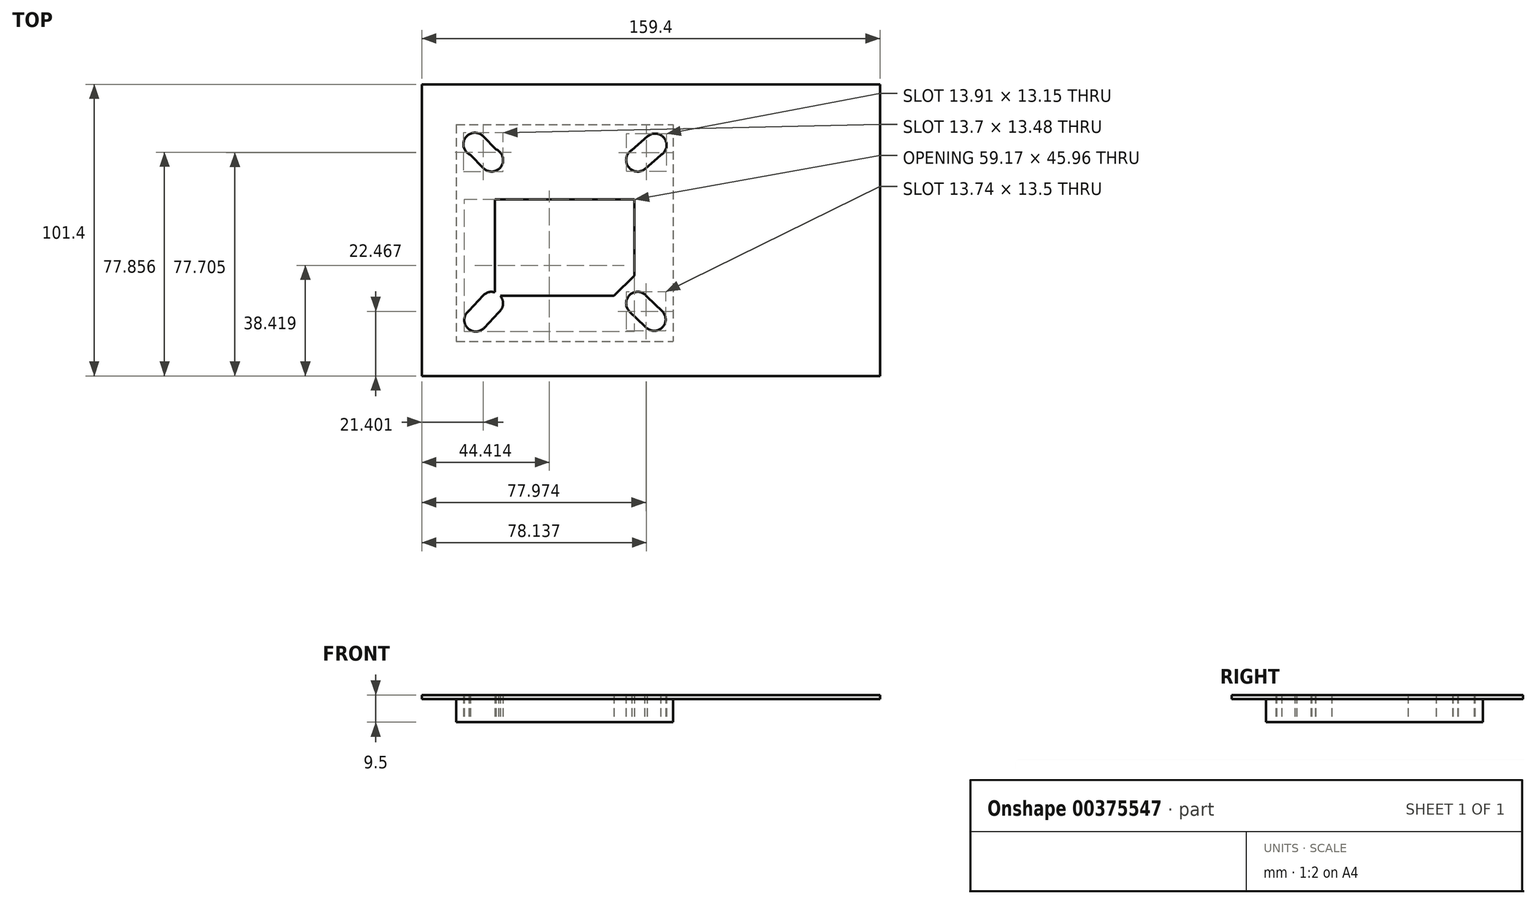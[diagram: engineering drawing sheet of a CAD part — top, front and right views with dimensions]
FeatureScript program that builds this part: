
annotation { "Feature Type Name" : "Feature", "Feature Type Description" : "" }
export const myFeature = defineFeature(function(context is Context, id is Id, definition is map)
    precondition{}
    {
        {
            var Q0;
            Q0=qCreatedBy(makeId("Top.planeOp"),FACE);
            var sketch = newSketch(context, id + "F0", { "sketchPlane" : qUnion([Q0])});
            skLineSegment(sketch, "E0.bottom", {"start": v(-37.22, 52.6) * mm, "end": v(38.18, 52.6) * mm});
            skLineSegment(sketch, "E0.top", {"start": v(-37.22, -22.8) * mm, "end": v(38.18, -22.8) * mm});
            skLineSegment(sketch, "E0.left", {"start": v(-37.22, 52.6) * mm, "end": v(-37.22, -22.8) * mm});
            skLineSegment(sketch, "E0.right", {"start": v(38.18, 52.6) * mm, "end": v(38.18, -22.8) * mm});
            skLineSegment(sketch, "E1.bottom", {"start": v(-23.82, 26.6) * mm, "end": v(24.78, 26.6) * mm});
            skLineSegment(sketch, "E1.left", {"start": v(-23.82, 26.6) * mm, "end": v(-23.82, -6.93) * mm});
            skCircle(sketch, "E2", {"center": v(-24.92, 40.3) * mm, "radius": 4 * mm});
            skCircle(sketch, "E3", {"center": v(25.88, 40.3) * mm, "radius": 4 * mm});
            skCircle(sketch, "E4", {"center": v(25.88, -9.56) * mm, "radius": 4 * mm});
            skCircle(sketch, "E5", {"center": v(-24.92, -9.56) * mm, "radius": 4 * mm});
            skLineSegment(sketch, "E6", {"start": v(24.78, 0) * mm, "end": v(17.57, -6.93) * mm});
            skLineSegment(sketch, "E7", {"start": v(24.78, 26.6) * mm, "end": v(24.78, 0) * mm});
            skLineSegment(sketch, "E8", {"start": v(17.57, -6.93) * mm, "end": v(-23.82, -6.93) * mm});
            skCircle(sketch, "E9", {"center": v(31.63, -15.13) * mm, "radius": 4 * mm});
            skCircle(sketch, "E10", {"center": v(-30.42, -15.37) * mm, "radius": 4 * mm});
            skCircle(sketch, "E11", {"center": v(-30.72, 45.8) * mm, "radius": 4 * mm});
            skCircle(sketch, "E12", {"center": v(31.95, 45.5) * mm, "radius": 4 * mm});
            skLineSegment(sketch, "E13", {"start": v(29.52, -18.53) * mm, "end": v(23.13, -12.46) * mm});
            skLineSegment(sketch, "E14", {"start": v(27.99, -6.16) * mm, "end": v(34.38, -12.23) * mm});
            skLineSegment(sketch, "E15", {"start": v(-21.53, -11.68) * mm, "end": v(-27.48, -18.1) * mm});
            skLineSegment(sketch, "E16", {"start": v(-33.8, -13.25) * mm, "end": v(-27.85, -6.84) * mm});
            skLineSegment(sketch, "E17", {"start": v(28.52, 37.28) * mm, "end": v(35.14, 43.08) * mm});
            skLineSegment(sketch, "E18", {"start": v(22.7, 42.71) * mm, "end": v(29.32, 48.5) * mm});
            skLineSegment(sketch, "E19", {"start": v(-23.34, 43.97) * mm, "end": v(-27.86, 48.6) * mm});
            skLineSegment(sketch, "E20", {"start": v(-27.78, 37.5) * mm, "end": v(-32.3, 42.12) * mm});
            skSolve(sketch);
        }
        {
            var Q0;
            Q0=makeQuery(id+"F0.imprint","IMPRINT",FACE,{"disambiguationData":[TD([[makeQuery(id+"F0.imprint","IMPRINT",EDGE,{"derivedFrom":sQuery(id+"F0.wireOp",EDGE,"E0.bottom")}),-1.0]])]});
            extrude(context, id + "F1", {"entities" : qUnion([Q0]), "depth" : 8 * mm});
        }
        {
            var Q0;
            Q0=makeQuery(id+"F1.opExtrude","CAP_FACE",FACE,{"disambiguationData":[OSD([sQuery(id+"F0.wireOp",EDGE,"E0.bottom"),sQuery(id+"F0.wireOp",EDGE,"E0.top"),sQuery(id+"F0.wireOp",EDGE,"E0.left"),sQuery(id+"F0.wireOp",EDGE,"E0.right"),sQuery(id+"F0.wireOp",EDGE,"E1.bottom"),sQuery(id+"F0.wireOp",EDGE,"E1.left"),sQuery(id+"F0.wireOp",EDGE,"E2"),sQuery(id+"F0.wireOp",EDGE,"E3"),sQuery(id+"F0.wireOp",EDGE,"E4"),sQuery(id+"F0.wireOp",EDGE,"E5"),sQuery(id+"F0.wireOp",EDGE,"E6"),sQuery(id+"F0.wireOp",EDGE,"E7"),sQuery(id+"F0.wireOp",EDGE,"E8")])],"isStart":false});
            var sketch = newSketch(context, id + "F2", { "sketchPlane" : qUnion([Q0])});
            skLineSegment(sketch, "E21.bottom", {"start": v(-49.22, 66.6) * mm, "end": v(110.18, 66.6) * mm});
            skLineSegment(sketch, "E21.top", {"start": v(-49.22, -34.8) * mm, "end": v(110.18, -34.8) * mm});
            skLineSegment(sketch, "E21.left", {"start": v(-49.22, 66.6) * mm, "end": v(-49.22, -34.8) * mm});
            skLineSegment(sketch, "E21.right", {"start": v(110.18, 66.6) * mm, "end": v(110.18, -34.8) * mm});
            skSolve(sketch);
        }
        {
            var Q0;
            Q0=makeQuery(id+"F2.imprint","IMPRINT",FACE,{"disambiguationData":[TD([[makeQuery(id+"F2.imprint","IMPRINT",EDGE,{"derivedFrom":sQuery(id+"F2.wireOp",EDGE,"E21.bottom")}),-1.0]])]});
            var Q1;
            Q1=makeQuery(id+"F2.imprint","IMPRINT",FACE,{"disambiguationData":[TD([[makeQuery(id+"F2.imprint","IMPRINT",EDGE,{"derivedFrom":makeQuery(id+"F1.opExtrude","CAP_EDGE",EDGE,{"disambiguationData":[OSD([sQuery(id+"F0.wireOp",EDGE,"E0.bottom")])],"isStart":false})}),-1.0]])]});
            extrude(context, id + "F3", {"entities" : qUnion([Q0, Q1]), "operationType" : NewBodyOperationType.ADD, "depth" : 1.5 * mm});
        }
    });
